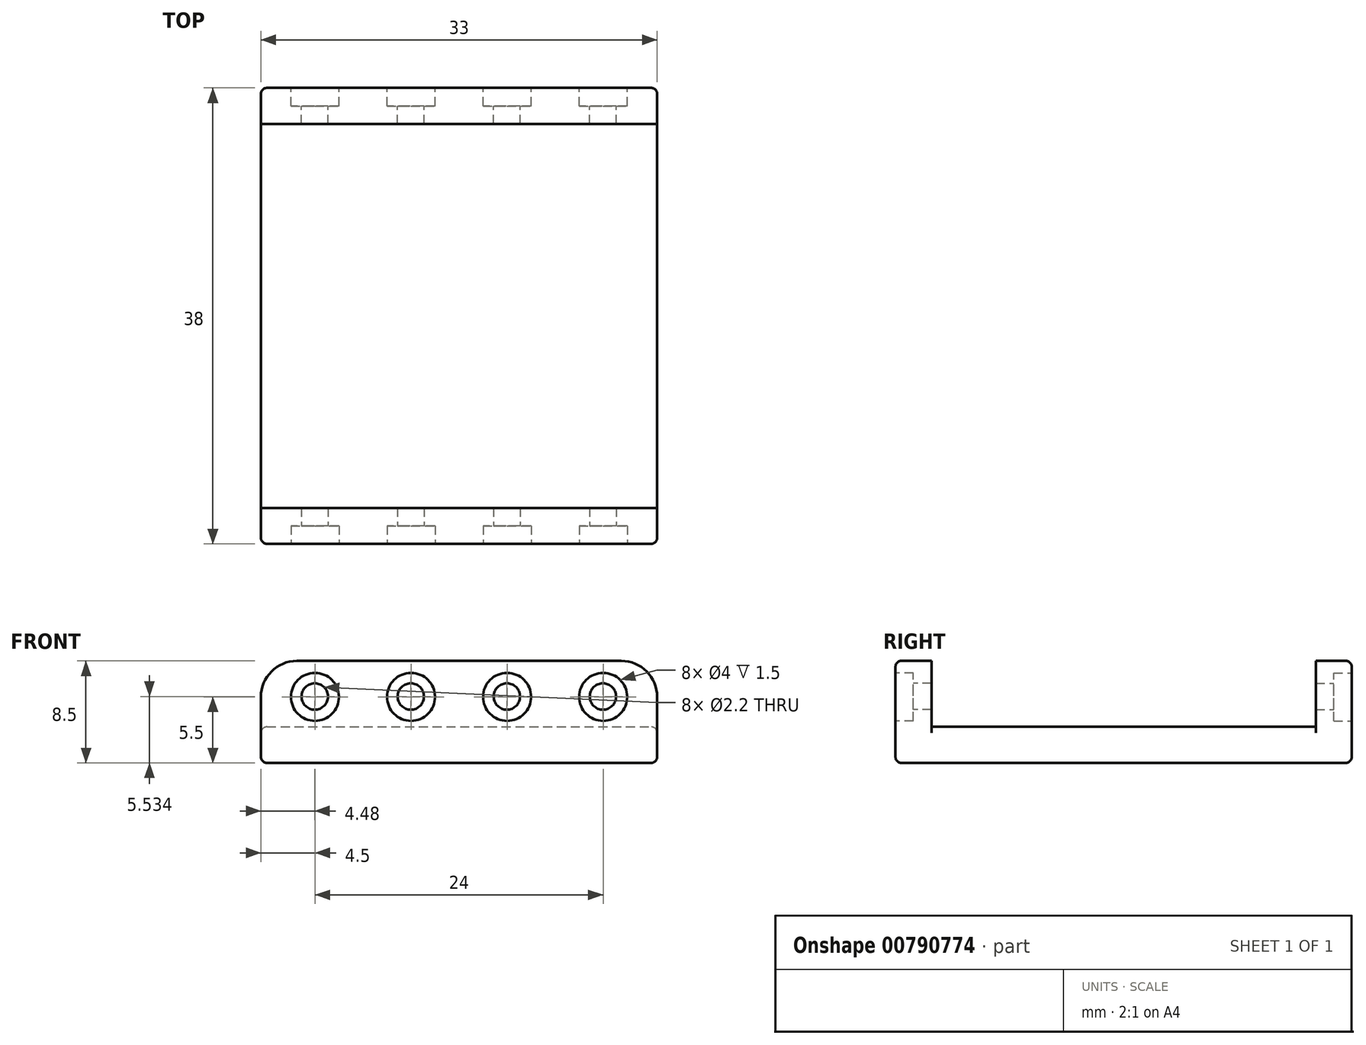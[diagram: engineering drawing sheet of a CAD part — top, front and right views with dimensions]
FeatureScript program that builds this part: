
annotation { "Feature Type Name" : "Feature", "Feature Type Description" : "" }
export const myFeature = defineFeature(function(context is Context, id is Id, definition is map)
    precondition{}
    {
        {
            var Q0;
            Q0=qCreatedBy(makeId("Front.planeOp"),FACE);
            var sketch = newSketch(context, id + "F0", { "sketchPlane" : qUnion([Q0])});
            skLineSegment(sketch, "E0.bottom", {"start": v(-13.5, 8.5) * mm, "end": v(13.5, 8.5) * mm});
            skLineSegment(sketch, "E0.top", {"start": v(-16.5, 0) * mm, "end": v(16.5, 0) * mm});
            skLineSegment(sketch, "E0.left", {"start": v(-16.5, 5.5) * mm, "end": v(-16.5, 0) * mm});
            skLineSegment(sketch, "E0.right", {"start": v(16.5, 5.5) * mm, "end": v(16.5, 0) * mm});
            skPoint(sketch, "E1.visualSharp", {"position": v(-16.5, 8.5) * mm});
            skArc(sketch, "E1.filletArc", {"start": v(-13.5, 8.5) * mm, "mid": v(-15.62, 7.62) * mm, "end": v(-16.5, 5.5) * mm});
            skPoint(sketch, "E2.visualSharp", {"position": v(16.5, 8.5) * mm});
            skArc(sketch, "E2.filletArc", {"start": v(16.5, 5.5) * mm, "mid": v(15.62, 7.62) * mm, "end": v(13.5, 8.5) * mm});
            skSolve(sketch);
        }
        {
            var Q0;
            Q0=qCreatedBy(makeId("Front.planeOp"),FACE);
            var sketch = newSketch(context, id + "F1", { "sketchPlane" : qUnion([Q0])});
            skCircle(sketch, "E3", {"center": v(-12, 5.5) * mm, "radius": 2 * mm});
            skCircle(sketch, "E4.1.0.0", {"center": v(-4, 5.5) * mm, "radius": 2 * mm});
            skCircle(sketch, "E4.2.0.0", {"center": v(4, 5.5) * mm, "radius": 2 * mm});
            skCircle(sketch, "E4.3.0.0", {"center": v(12, 5.5) * mm, "radius": 2 * mm});
            skLineSegment(sketch, "E4.direction1", {"start": v(-12, 5.5) * mm, "end": v(-4, 5.5) * mm, "construction": true});
            skSolve(sketch);
        }
        {
            var Q0;
            Q0=qCreatedBy(makeId("Front.planeOp"),FACE);
            var sketch = newSketch(context, id + "F2", { "sketchPlane" : qUnion([Q0])});
            skCircle(sketch, "E5", {"center": v(-12.02, 5.53) * mm, "radius": 1.1 * mm});
            skCircle(sketch, "E6.1.0.0", {"center": v(-4.02, 5.53) * mm, "radius": 1.1 * mm});
            skCircle(sketch, "E6.2.0.0", {"center": v(3.98, 5.53) * mm, "radius": 1.1 * mm});
            skCircle(sketch, "E6.3.0.0", {"center": v(11.98, 5.53) * mm, "radius": 1.1 * mm});
            skLineSegment(sketch, "E6.direction1", {"start": v(-12.02, 5.53) * mm, "end": v(-4.02, 5.53) * mm, "construction": true});
            skSolve(sketch);
        }
        {
            var Q0;
            Q0=qCreatedBy(makeId("Front.planeOp"),FACE);
            var sketch = newSketch(context, id + "F3", { "sketchPlane" : qUnion([Q0])});
            skLineSegment(sketch, "E7.bottom", {"start": v(-16.5, 3) * mm, "end": v(16.5, 3) * mm});
            skLineSegment(sketch, "E7.top", {"start": v(-16.5, 0) * mm, "end": v(16.5, 0) * mm});
            skLineSegment(sketch, "E7.left", {"start": v(-16.5, 3) * mm, "end": v(-16.5, 0) * mm});
            skLineSegment(sketch, "E7.right", {"start": v(16.5, 3) * mm, "end": v(16.5, 0) * mm});
            skSolve(sketch);
        }
        {
            var Q0;
            Q0 = qSketchRegion(id + "F0", true);
            extrude(context, id + "F4", {"entities" : qUnion([Q0]), "oppositeDirection" : true, "depth" : 3 * mm, "offsetDistance" : 25 * mm});
        }
        {
            var Q0;
            Q0 = qSketchRegion(id + "F1", true);
            extrude(context, id + "F5", {"entities" : qUnion([Q0]), "operationType" : NewBodyOperationType.REMOVE, "oppositeDirection" : true, "depth" : 1.5 * mm, "offsetDistance" : 25 * mm});
        }
        {
            var Q0;
            Q0 = qSketchRegion(id + "F2", true);
            extrude(context, id + "F6", {"entities" : qUnion([Q0]), "operationType" : NewBodyOperationType.REMOVE, "oppositeDirection" : true, "depth" : 3 * mm, "offsetDistance" : 25 * mm});
        }
        {
            var Q0;
            Q0 = qSketchRegion(id + "F3", true);
            extrude(context, id + "F7", {"entities" : qUnion([Q0]), "operationType" : NewBodyOperationType.ADD, "oppositeDirection" : true, "depth" : 19 * mm, "offsetDistance" : 25 * mm});
        }
        {
            var Q0;
            Q0=makeQuery(id+"F4.opExtrude","SWEPT_BODY",BODY,{"disambiguationData":[OSD([sQuery(id+"F0.wireOp",EDGE,"E0.bottom"),sQuery(id+"F0.wireOp",EDGE,"E0.top"),sQuery(id+"F0.wireOp",EDGE,"E0.left"),sQuery(id+"F0.wireOp",EDGE,"E0.right"),sQuery(id+"F0.wireOp",EDGE,"E1.filletArc"),sQuery(id+"F0.wireOp",EDGE,"E2.filletArc")])]});
            var Q1;
            Q1=makeQuery(id+"F7.opExtrude","CAP_FACE",FACE,{"disambiguationData":[OSD([sQuery(id+"F3.wireOp",EDGE,"E7.bottom"),sQuery(id+"F3.wireOp",EDGE,"E7.top"),sQuery(id+"F3.wireOp",EDGE,"E7.left"),sQuery(id+"F3.wireOp",EDGE,"E7.right")])],"isStart":false});
            mirror(context, id + "F8", {"operationType" : NewBodyOperationType.ADD, "entities" : qUnion([Q0]), "mirrorPlane" : qUnion([Q1])});
        }
        {
            var Q0;
            Q0=makeQuery(id+"F4.opExtrude","CAP_EDGE",EDGE,{"disambiguationData":[OSD([sQuery(id+"F0.wireOp",EDGE,"E0.bottom")])],"isStart":true});
            var Q1;
            Q1=makeQuery(id+"F8.opPattern","COPY",EDGE,{"derivedFrom":makeQuery(id+"F4.opExtrude","CAP_EDGE",EDGE,{"disambiguationData":[OSD([sQuery(id+"F0.wireOp",EDGE,"E0.bottom")])],"isStart":true}),"instanceName":"1"});
            var Q2;
            {var subQ0=makeQuery(id+"F7.opExtrude","SWEPT_EDGE",EDGE,{"disambiguationData":[OSD([sQuery(id+"F3.wireOp",EDGE,"E7.bottom"),sQuery(id+"F3.wireOp",EDGE,"E7.right")])]});Q2=makeQuery(id+"F8.boolean.opBoolean","MERGE",EDGE,{"derivedFrom":[subQ0,makeQuery(id+"F8.opPattern","COPY",EDGE,{"derivedFrom":subQ0,"instanceName":"1"})]});}
            var Q3;
            {var subQ0=makeQuery(id+"F7.opExtrude","SWEPT_EDGE",EDGE,{"disambiguationData":[OSD([sQuery(id+"F3.wireOp",EDGE,"E7.bottom"),sQuery(id+"F3.wireOp",EDGE,"E7.left")])]});Q3=makeQuery(id+"F8.boolean.opBoolean","MERGE",EDGE,{"derivedFrom":[subQ0,makeQuery(id+"F8.opPattern","COPY",EDGE,{"derivedFrom":subQ0,"instanceName":"1"})]});}
            fillet(context, id + "F9", {"entities" : qUnion([Q0, Q1, Q2, Q3]), "radius" : 0.5 * mm, "tangentPropagation" : true, "allowEdgeOverflow" : false});
        }
        {
            var Q0;
            {var subQ0=makeQuery(id+"F7.boolean.opBoolean","MERGE",FACE,{"derivedFrom":[makeQuery(id+"F4.opExtrude","SWEPT_FACE",FACE,{"disambiguationData":[OSD([sQuery(id+"F0.wireOp",EDGE,"E0.top")])]}),makeQuery(id+"F7.opExtrude","SWEPT_FACE",FACE,{"disambiguationData":[OSD([sQuery(id+"F3.wireOp",EDGE,"E7.top")])]})]});Q0=makeQuery(id+"F8.boolean.opBoolean","MERGE",FACE,{"derivedFrom":[subQ0,makeQuery(id+"F8.opPattern","COPY",FACE,{"derivedFrom":subQ0,"instanceName":"1"})]});}
            fillet(context, id + "F10", {"entities" : qUnion([Q0]), "radius" : 0.5 * mm, "tangentPropagation" : true, "allowEdgeOverflow" : false});
        }
    });
